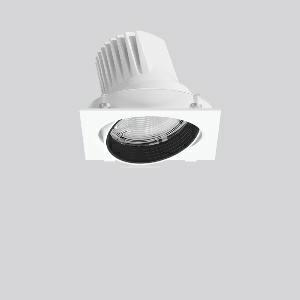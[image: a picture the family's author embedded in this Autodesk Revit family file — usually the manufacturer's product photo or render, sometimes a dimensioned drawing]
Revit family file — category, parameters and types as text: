
# Revit family: magcardo_maxi_722191_002_76_0004
name_source: partatom
category: Lighting Fixtures
units: mm (PartAtom-declared; Revit-internal decimal feet)

## family parameters
Cut with Voids When Loaded = No
Host = Face
Light Source = No
Part Type = Normal
Room Calculation Point = No
Round Connector Dimension = Use Diameter
Shared = No

## types (1)
- MAGCARDO maxi (1 x LED Modul 930, 2750 lm, 3000)
    Apparent Load = 25 VA
    Approval mark = CE
    CIE Flux Codes = 96 100 100 100 100
    Color Rendering = 90
    Color Temperature = 3000
    Default Elevation = 1800 mm
    Description = Series: MAGCARDO maxi
Projector unit for tool-free mounting in separate recessed frame. Luminaire top: die-cast aluminium, powder-coated. Rotation range 356° and swivel range ± 35°. Inner cover prevents view into the false ceiling. Black plastic ring and recessed LED to prevent glare from the side. Optical assembly with lens made of plastic (polycarbonate) for the best homogeneous light distribution - can be changed without tools. Best colour rendering index Ra>90. Magnetic click locking mechanism for quick and convenient installation without tools: insert the recessed frame (1, 2 or 3-lamp) with clamp fastener (no tools required), push the luminaire head with the base plate into the recessed frame and fix magnetically. Including separate LED converter with connecting cable 600 mm.High quality converter without flickering and stroboscopic effect. Through-wiring box (5 pole) available as accessory. The following accessories can be mounted without use of tools: interchangeable lenses, honeycomb louvre, clear and frosted diffusers, white interchangeable plastic ring.Modular design: recessed mounting frame must be ordered separately! 
Colour: traffic white, matt (RAL 9016)
Length: 172 mm
Width: 167 mm
Height: 137 mm
Recess height: 155 mm
Lamp: LED
Socket: without socket
Colour temperature: 3000K
Colour rendering index (CRI): 92
System power: 25 W
Rated luminous flux: 2750 lm
Luminous efficiency: 110 lm/W
Control gear: Converter, dimmable, DALI
Protection class: II
Type of protection: IP 20
    Height = 0 mm  [stored 0 ft]
    Lamp = 1 x LED Modul 930
    Lamp Light Flux = 2750 lm
    Lamp count = 1
    Length = 172 mm
    Lifetime = 50000 h
    Luminous efficacy = 110 lm/W
    Manufacturer = RZB
    ModVariant = No
    Model = 722191.002.76
    Mounting Place = Ceiling, Wall
    Mounting Type = Recessed
    Number of Poles = 1
    OnlyDefault = Yes
    Power Factor = 1
    Product Name = MAGCARDO maxi
    Product group = Recessed projectors
    ProductGroupID = 401
    Protection Class = Protection class II
    Protection Degree = IP 20
    RLX_Detail_Level = 1
    RLX_Emergency_Light_Flux = 0 lm
    RLX_Emergency_Type = 0
    RLX_Emergency_Type_DB = No
    RlxData = <blob elided: 40585 chars, md5=1d1ddf96>
    Socket = socket
    Standby Power = 0 W
    System Light Flux = 2750 lm
    System Power = 25 W
    Type Comments = Product without accessories
    Type Image = 722048.002.jpg
    URL = http://relux.com
    VarID = ---
    Voltage = 230 V
    Voltage Range = 220-240 V
    Weight = 0.00 kg
    Width = 167 mm

note: [stored X ft] marks values corroborated as IEEE doubles in the binary element streams (Revit-internal decimal feet)

## geometry (parser evidence)
native form markers: Blend x4, Sweep x12
no freeform markers — native parametric forms only
